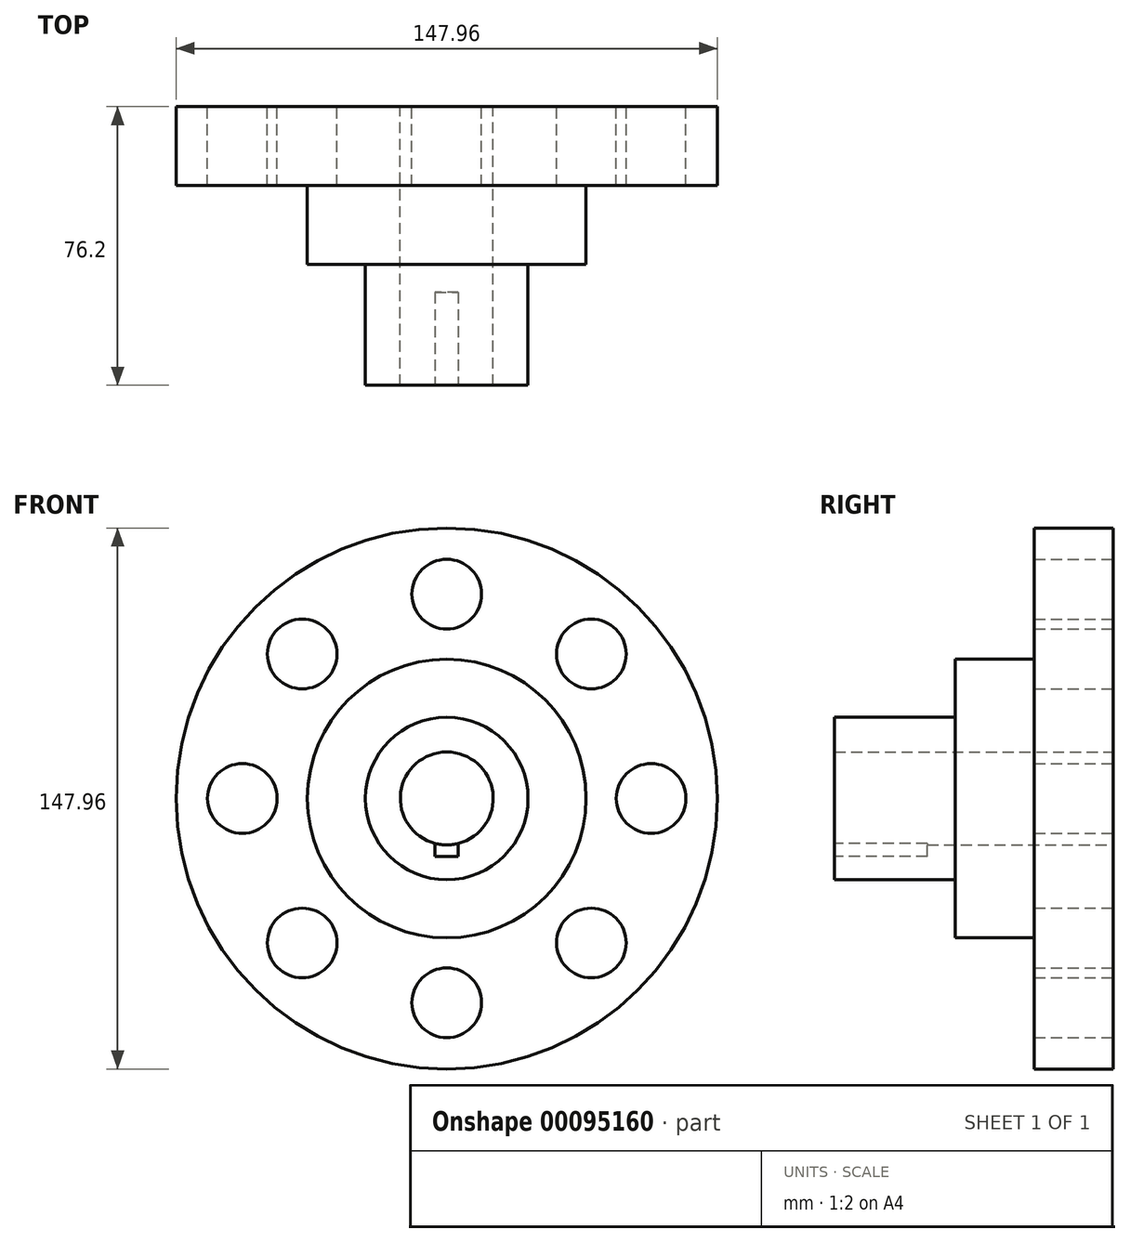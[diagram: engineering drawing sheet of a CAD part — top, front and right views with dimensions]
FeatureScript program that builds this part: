
annotation { "Feature Type Name" : "Feature", "Feature Type Description" : "" }
export const myFeature = defineFeature(function(context is Context, id is Id, definition is map)
    precondition{}
    {
        {
            var Q0;
            Q0=qCreatedBy(makeId("Front.planeOp"),FACE);
            var sketch = newSketch(context, id + "F0", { "sketchPlane" : qUnion([Q0])});
            skCircle(sketch, "E0", {"center": v(0, 0) * mm, "radius": 12.7 * mm});
            skCircle(sketch, "E1", {"center": v(0, 0) * mm, "radius": 22.23 * mm});
            skCircle(sketch, "E2", {"center": v(0, 0) * mm, "radius": 38.1 * mm});
            skCircle(sketch, "E3", {"center": v(0, 0) * mm, "radius": 55.88 * mm});
            skCircle(sketch, "E4", {"center": v(0, 0) * mm, "radius": 73.98 * mm});
            skLineSegment(sketch, "E5.bottom", {"start": v(3.17, -15.88) * mm, "end": v(-3.18, -15.88) * mm});
            skLineSegment(sketch, "E5.top", {"start": v(3.17, -9.53) * mm, "end": v(-3.18, -9.53) * mm});
            skLineSegment(sketch, "E5.left", {"start": v(3.17, -15.88) * mm, "end": v(3.17, -9.53) * mm});
            skLineSegment(sketch, "E5.right", {"start": v(-3.18, -15.88) * mm, "end": v(-3.18, -9.53) * mm});
            skPoint(sketch, "E5.middle", {"position": v(0, -12.7) * mm});
            skCircle(sketch, "E6", {"center": v(0, 55.88) * mm, "radius": 9.53 * mm});
            skCircle(sketch, "E7", {"center": v(55.88, 0) * mm, "radius": 9.53 * mm});
            skCircle(sketch, "E8", {"center": v(0, -55.88) * mm, "radius": 9.53 * mm});
            skCircle(sketch, "E9", {"center": v(-55.88, 0) * mm, "radius": 9.53 * mm});
            skLineSegment(sketch, "E10", {"start": v(0, 0) * mm, "end": v(39.51, 39.51) * mm});
            skLineSegment(sketch, "E11", {"start": v(0, 0) * mm, "end": v(-39.51, -39.51) * mm});
            skLineSegment(sketch, "E12", {"start": v(0, 0) * mm, "end": v(-39.51, 39.51) * mm});
            skLineSegment(sketch, "E13", {"start": v(0, 0) * mm, "end": v(39.51, -39.51) * mm});
            skCircle(sketch, "E14", {"center": v(39.51, 39.51) * mm, "radius": 9.53 * mm});
            skCircle(sketch, "E15", {"center": v(-39.51, 39.51) * mm, "radius": 9.53 * mm});
            skCircle(sketch, "E16", {"center": v(-39.51, -39.51) * mm, "radius": 9.53 * mm});
            skCircle(sketch, "E17", {"center": v(39.51, -39.51) * mm, "radius": 9.53 * mm});
            skSolve(sketch);
        }
        {
            var Q0;
            Q0=makeQuery(id+"F0.imprint","IMPRINT",FACE,{"disambiguationData":[TD([[makeQuery(id+"F0.imprint","IMPRINT",EDGE,{"derivedFrom":sQuery(id+"F0.wireOp",EDGE,"E4")}),1.0]])]});
            extrude(context, id + "F1", {"entities" : qUnion([Q0]), "depth" : 21.59 * mm});
        }
        {
            var Q0;
            {var subQ6=sQuery(id+"F0.wireOp",EDGE,"E12");var subQ7=sQuery(id+"F0.wireOp",EDGE,"E2");var subQ8=makeQuery(id+"F0.imprint","INTERSECT",VERTEX,{"derivedFrom":[subQ7,subQ6]});Q0=makeQuery(id+"F0.imprint","IMPRINT",FACE,{"disambiguationData":[TD([[makeQuery(id+"F0.imprint","IMPRINT",EDGE,{"disambiguationData":[TD([[subQ8,-1.0]])],"derivedFrom":subQ7}),-1.0]])]});}
            var Q1;
            {var subQ8=sQuery(id+"F0.wireOp",EDGE,"E12");var subQ9=sQuery(id+"F0.wireOp",EDGE,"E2");var subQ10=makeQuery(id+"F0.imprint","INTERSECT",VERTEX,{"derivedFrom":[subQ9,subQ8]});Q1=makeQuery(id+"F0.imprint","IMPRINT",FACE,{"disambiguationData":[TD([[makeQuery(id+"F0.imprint","IMPRINT",EDGE,{"disambiguationData":[TD([[subQ10,1.0]])],"derivedFrom":subQ9}),-1.0]])]});}
            var Q2;
            {var subQ5=sQuery(id+"F0.wireOp",EDGE,"E10");var subQ6=sQuery(id+"F0.wireOp",EDGE,"E2");var subQ7=makeQuery(id+"F0.imprint","INTERSECT",VERTEX,{"derivedFrom":[subQ6,subQ5]});Q2=makeQuery(id+"F0.imprint","IMPRINT",FACE,{"disambiguationData":[TD([[makeQuery(id+"F0.imprint","IMPRINT",EDGE,{"disambiguationData":[TD([[subQ7,1.0]])],"derivedFrom":subQ6}),-1.0]])]});}
            var Q3;
            {var subQ8=sQuery(id+"F0.wireOp",EDGE,"E11");var subQ9=sQuery(id+"F0.wireOp",EDGE,"E2");var subQ10=makeQuery(id+"F0.imprint","INTERSECT",VERTEX,{"derivedFrom":[subQ9,subQ8]});Q3=makeQuery(id+"F0.imprint","IMPRINT",FACE,{"disambiguationData":[TD([[makeQuery(id+"F0.imprint","IMPRINT",EDGE,{"disambiguationData":[TD([[subQ10,-1.0]])],"derivedFrom":subQ9}),-1.0]])]});}
            extrude(context, id + "F2", {"entities" : qUnion([Q0, Q1, Q2, Q3]), "operationType" : NewBodyOperationType.ADD, "depth" : 21.59 * mm});
        }
        {
            var Q0;
            {var subQ0=sQuery(id+"F0.wireOp",EDGE,"E12");var subQ1=sQuery(id+"F0.wireOp",EDGE,"E1");var subQ2=makeQuery(id+"F0.imprint","INTERSECT",VERTEX,{"derivedFrom":[subQ1,subQ0]});Q0=makeQuery(id+"F0.imprint","IMPRINT",FACE,{"disambiguationData":[TD([[makeQuery(id+"F0.imprint","IMPRINT",EDGE,{"disambiguationData":[TD([[subQ2,1.0]])],"derivedFrom":subQ1}),-1.0]])]});}
            var Q1;
            {var subQ0=sQuery(id+"F0.wireOp",EDGE,"E10");var subQ1=sQuery(id+"F0.wireOp",EDGE,"E1");var subQ2=makeQuery(id+"F0.imprint","INTERSECT",VERTEX,{"derivedFrom":[subQ1,subQ0]});Q1=makeQuery(id+"F0.imprint","IMPRINT",FACE,{"disambiguationData":[TD([[makeQuery(id+"F0.imprint","IMPRINT",EDGE,{"disambiguationData":[TD([[subQ2,1.0]])],"derivedFrom":subQ1}),-1.0]])]});}
            var Q2;
            {var subQ0=sQuery(id+"F0.wireOp",EDGE,"E11");var subQ1=sQuery(id+"F0.wireOp",EDGE,"E1");var subQ2=makeQuery(id+"F0.imprint","INTERSECT",VERTEX,{"derivedFrom":[subQ1,subQ0]});Q2=makeQuery(id+"F0.imprint","IMPRINT",FACE,{"disambiguationData":[TD([[makeQuery(id+"F0.imprint","IMPRINT",EDGE,{"disambiguationData":[TD([[subQ2,-1.0]])],"derivedFrom":subQ1}),-1.0]])]});}
            var Q3;
            {var subQ0=sQuery(id+"F0.wireOp",EDGE,"E12");var subQ1=sQuery(id+"F0.wireOp",EDGE,"E1");var subQ2=makeQuery(id+"F0.imprint","INTERSECT",VERTEX,{"derivedFrom":[subQ1,subQ0]});Q3=makeQuery(id+"F0.imprint","IMPRINT",FACE,{"disambiguationData":[TD([[makeQuery(id+"F0.imprint","IMPRINT",EDGE,{"disambiguationData":[TD([[subQ2,-1.0]])],"derivedFrom":subQ1}),-1.0]])]});}
            extrude(context, id + "F3", {"entities" : qUnion([Q0, Q1, Q2, Q3]), "operationType" : NewBodyOperationType.ADD, "depth" : 43.18 * mm});
        }
        {
            var Q0;
            {var subQ0=sQuery(id+"F0.wireOp",EDGE,"E12");var subQ1=sQuery(id+"F0.wireOp",EDGE,"E0");var subQ2=makeQuery(id+"F0.imprint","INTERSECT",VERTEX,{"derivedFrom":[subQ1,subQ0]});Q0=makeQuery(id+"F0.imprint","IMPRINT",FACE,{"disambiguationData":[TD([[makeQuery(id+"F0.imprint","IMPRINT",EDGE,{"disambiguationData":[TD([[subQ2,1.0]])],"derivedFrom":subQ1}),-1.0]])]});}
            var Q1;
            {var subQ0=sQuery(id+"F0.wireOp",EDGE,"E10");var subQ1=sQuery(id+"F0.wireOp",EDGE,"E0");var subQ2=makeQuery(id+"F0.imprint","INTERSECT",VERTEX,{"derivedFrom":[subQ1,subQ0]});Q1=makeQuery(id+"F0.imprint","IMPRINT",FACE,{"disambiguationData":[TD([[makeQuery(id+"F0.imprint","IMPRINT",EDGE,{"disambiguationData":[TD([[subQ2,1.0]])],"derivedFrom":subQ1}),-1.0]])]});}
            var Q2;
            {var subQ5=sQuery(id+"F0.wireOp",EDGE,"E5.bottom");Q2=makeQuery(id+"F0.imprint","IMPRINT",FACE,{"disambiguationData":[TD([[makeQuery(id+"F0.imprint","IMPRINT",EDGE,{"derivedFrom":subQ5}),1.0]])]});}
            var Q3;
            {var subQ0=sQuery(id+"F0.wireOp",EDGE,"E12");var subQ1=sQuery(id+"F0.wireOp",EDGE,"E0");var subQ2=makeQuery(id+"F0.imprint","INTERSECT",VERTEX,{"derivedFrom":[subQ1,subQ0]});Q3=makeQuery(id+"F0.imprint","IMPRINT",FACE,{"disambiguationData":[TD([[makeQuery(id+"F0.imprint","IMPRINT",EDGE,{"disambiguationData":[TD([[subQ2,-1.0]])],"derivedFrom":subQ1}),-1.0]])]});}
            var Q4;
            {var subQ5=sQuery(id+"F0.wireOp",EDGE,"E5.bottom");Q4=makeQuery(id+"F0.imprint","IMPRINT",FACE,{"disambiguationData":[TD([[makeQuery(id+"F0.imprint","IMPRINT",EDGE,{"derivedFrom":subQ5}),-1.0]])]});}
            extrude(context, id + "F4", {"entities" : qUnion([Q0, Q1, Q2, Q3, Q4]), "operationType" : NewBodyOperationType.ADD, "depth" : 76.2 * mm});
        }
        {
            var Q0;
            Q0=makeQuery(id+"F4.opExtrude","CAP_FACE",FACE,{"disambiguationData":[OSD([sQuery(id+"F0.wireOp",EDGE,"E0"),sQuery(id+"F0.wireOp",EDGE,"E1")])],"isStart":false});
            var sketch = newSketch(context, id + "F5", { "sketchPlane" : qUnion([Q0])});
            skLineSegment(sketch, "E18.bottom", {"start": v(3.17, -15.88) * mm, "end": v(-3.18, -15.88) * mm});
            skLineSegment(sketch, "E18.top", {"start": v(3.18, -9.53) * mm, "end": v(-3.18, -9.53) * mm});
            skLineSegment(sketch, "E18.left", {"start": v(3.17, -15.88) * mm, "end": v(3.18, -9.53) * mm});
            skLineSegment(sketch, "E18.right", {"start": v(-3.18, -15.88) * mm, "end": v(-3.18, -9.53) * mm});
            skPoint(sketch, "E18.middle", {"position": v(0, -12.7) * mm});
            skSolve(sketch);
        }
        {
            var Q0;
            {var subQ0=sQuery(id+"F5.wireOp",EDGE,"E18.bottom");Q0=makeQuery(id+"F5.imprint","IMPRINT",FACE,{"disambiguationData":[TD([[makeQuery(id+"F5.imprint","IMPRINT",EDGE,{"derivedFrom":subQ0}),-1.0]])]});}
            extrude(context, id + "F6", {"entities" : qUnion([Q0]), "operationType" : NewBodyOperationType.REMOVE, "oppositeDirection" : true, "depth" : 25.4 * mm});
        }
    });
